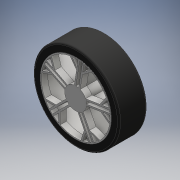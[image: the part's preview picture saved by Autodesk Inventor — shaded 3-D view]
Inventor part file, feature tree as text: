
AUTODESK INVENTOR PART (.ipt)
format: ipt  version: 2016 (Build 200138000, 138)  size: 374,272 bytes
history: native  units: mm
features: extrude x5, sketch x5, fillet x2, other x1
ambient origin geometry x8: Origin, YZ Plane, XZ Plane, XY Plane, X Axis, Y Axis, Z Axis, Center Point
bodies: Body1 (feature_tree)
feature tree (13):
  other  "Sólido1"
  extrude  "Extrusión1"  Depth=2.0mm TaperAngle=0.0deg
  extrude  "Extrusión5"  Depth=7.0mm TaperAngle=0.0deg
  extrude  "Extrusión6"  Depth=1.9mm TaperAngle=0.0deg
  extrude  "Extrusión7"  Depth=6.5mm
  extrude  "Extrusión8"  Depth=0.5mm
  fillet  "Empalme1"  Radius=0.5mm
  fillet  "Empalme2"  [1 undecoded]
  sketch  "Boceto1"  dims[d16=50.0mm d18=360.0deg d22=2.0mm d23=0.0mm]
  sketch  "Boceto7"  dims[d31=27.0mm d32=7.0mm d33=0.0mm]
  sketch  "Boceto8"  dims[d34=27.0mm d35=1.9mm d36=0.0mm]
  sketch  "Boceto9"  dims[d37=6.5mm d38=0.0mm d39=5.0mm]
  sketch  "Boceto10"  dims[d40=6.5mm d41=0.0mm d42=0.5mm d43=0.5mm]
note: 1 required parameter value undecoded (feature->parameter linkage not recoverable at this tier; creation-order binding heuristic only, values carry confidence <= 0.55)
